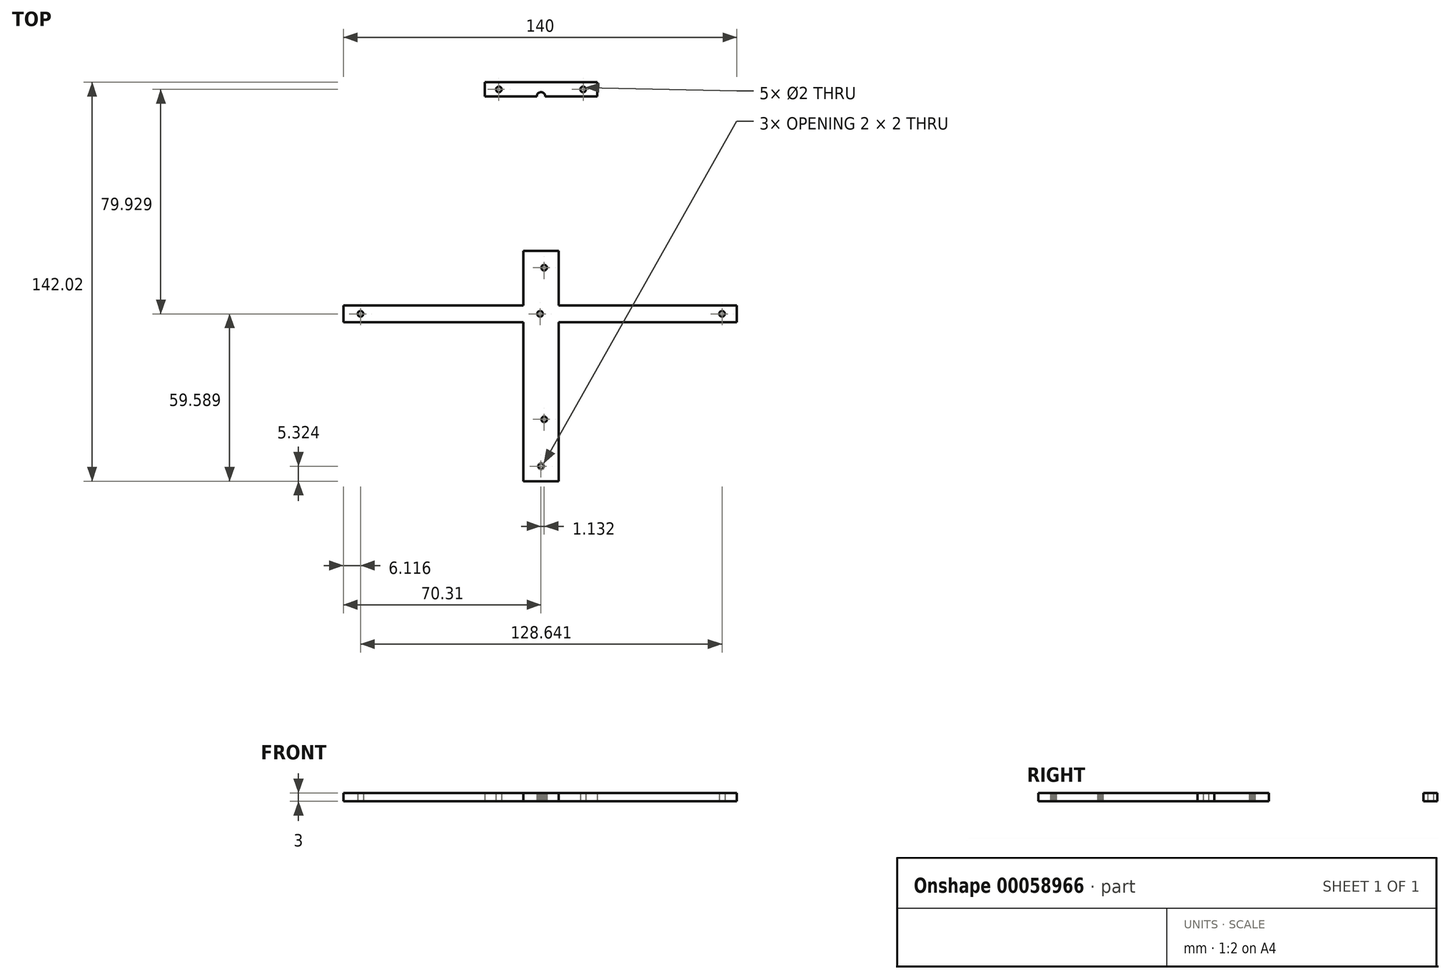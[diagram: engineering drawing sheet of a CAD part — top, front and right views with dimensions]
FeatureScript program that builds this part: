
annotation { "Feature Type Name" : "Feature", "Feature Type Description" : "" }
export const myFeature = defineFeature(function(context is Context, id is Id, definition is map)
    precondition{}
    {
        {
            var Q0;
            Q0=qCreatedBy(makeId("Top.planeOp"),FACE);
            var sketch = newSketch(context, id + "F0", { "sketchPlane" : qUnion([Q0])});
            skLineSegment(sketch, "E0", {"start": v(0.84, 33.8) * mm, "end": v(0.83, 33.92) * mm});
            skLineSegment(sketch, "E1", {"start": v(0.83, 33.92) * mm, "end": v(0.81, 34.04) * mm});
            skLineSegment(sketch, "E2", {"start": v(0.81, 34.04) * mm, "end": v(0.77, 34.16) * mm});
            skLineSegment(sketch, "E3", {"start": v(0.77, 34.16) * mm, "end": v(0.72, 34.28) * mm});
            skLineSegment(sketch, "E4", {"start": v(0.72, 34.28) * mm, "end": v(0.65, 34.38) * mm});
            skLineSegment(sketch, "E5", {"start": v(0.65, 34.38) * mm, "end": v(0.57, 34.48) * mm});
            skLineSegment(sketch, "E6", {"start": v(0.57, 34.48) * mm, "end": v(0.48, 34.57) * mm});
            skLineSegment(sketch, "E7", {"start": v(0.48, 34.57) * mm, "end": v(0.38, 34.64) * mm});
            skLineSegment(sketch, "E8", {"start": v(0.38, 34.64) * mm, "end": v(0.27, 34.7) * mm});
            skLineSegment(sketch, "E9", {"start": v(0.27, 34.7) * mm, "end": v(0.15, 34.75) * mm});
            skLineSegment(sketch, "E10", {"start": v(0.15, 34.75) * mm, "end": v(0.03, 34.78) * mm});
            skLineSegment(sketch, "E11", {"start": v(0.03, 34.78) * mm, "end": v(-0.1, 34.8) * mm});
            skLineSegment(sketch, "E12", {"start": v(-0.1, 34.8) * mm, "end": v(-0.22, 34.8) * mm});
            skLineSegment(sketch, "E13", {"start": v(-0.22, 34.8) * mm, "end": v(-0.35, 34.78) * mm});
            skLineSegment(sketch, "E14", {"start": v(-0.35, 34.78) * mm, "end": v(-0.47, 34.75) * mm});
            skLineSegment(sketch, "E15", {"start": v(-0.58, 34.7) * mm, "end": v(-0.7, 34.64) * mm});
            skLineSegment(sketch, "E16", {"start": v(-0.7, 34.64) * mm, "end": v(-0.8, 34.57) * mm});
            skLineSegment(sketch, "E17", {"start": v(-0.8, 34.57) * mm, "end": v(-0.89, 34.48) * mm});
            skLineSegment(sketch, "E18", {"start": v(-0.89, 34.48) * mm, "end": v(-0.97, 34.38) * mm});
            skLineSegment(sketch, "E19", {"start": v(-0.97, 34.38) * mm, "end": v(-1.03, 34.28) * mm});
            skLineSegment(sketch, "E20", {"start": v(-1.03, 34.28) * mm, "end": v(-1.09, 34.16) * mm});
            skLineSegment(sketch, "E21", {"start": v(-1.09, 34.16) * mm, "end": v(-1.13, 34.04) * mm});
            skLineSegment(sketch, "E22", {"start": v(-1.13, 34.04) * mm, "end": v(-1.15, 33.92) * mm});
            skLineSegment(sketch, "E23", {"start": v(-1.15, 33.92) * mm, "end": v(-1.16, 33.8) * mm});
            skLineSegment(sketch, "E24", {"start": v(-1.16, 33.8) * mm, "end": v(-1.15, 33.67) * mm});
            skLineSegment(sketch, "E25", {"start": v(-1.15, 33.67) * mm, "end": v(-1.13, 33.55) * mm});
            skLineSegment(sketch, "E26", {"start": v(-1.13, 33.55) * mm, "end": v(-1.09, 33.43) * mm});
            skLineSegment(sketch, "E27", {"start": v(-1.09, 33.43) * mm, "end": v(-1.03, 33.31) * mm});
            skLineSegment(sketch, "E28", {"start": v(-1.03, 33.31) * mm, "end": v(-0.97, 33.2) * mm});
            skLineSegment(sketch, "E29", {"start": v(-0.97, 33.2) * mm, "end": v(-0.89, 33.11) * mm});
            skLineSegment(sketch, "E30", {"start": v(-0.89, 33.11) * mm, "end": v(-0.8, 33.03) * mm});
            skLineSegment(sketch, "E31", {"start": v(-0.8, 33.03) * mm, "end": v(-0.7, 32.95) * mm});
            skLineSegment(sketch, "E32", {"start": v(-0.7, 32.95) * mm, "end": v(-0.58, 32.9) * mm});
            skLineSegment(sketch, "E33", {"start": v(-0.58, 32.9) * mm, "end": v(-0.47, 32.85) * mm});
            skLineSegment(sketch, "E34", {"start": v(-0.47, 32.85) * mm, "end": v(-0.35, 32.81) * mm});
            skLineSegment(sketch, "E35", {"start": v(-0.35, 32.81) * mm, "end": v(-0.22, 32.8) * mm});
            skLineSegment(sketch, "E36", {"start": v(-0.22, 32.8) * mm, "end": v(-0.1, 32.8) * mm});
            skLineSegment(sketch, "E37", {"start": v(-0.1, 32.8) * mm, "end": v(0.03, 32.81) * mm});
            skLineSegment(sketch, "E38", {"start": v(0.03, 32.81) * mm, "end": v(0.15, 32.85) * mm});
            skLineSegment(sketch, "E39", {"start": v(0.15, 32.85) * mm, "end": v(0.27, 32.9) * mm});
            skLineSegment(sketch, "E40", {"start": v(0.27, 32.9) * mm, "end": v(0.38, 32.95) * mm});
            skLineSegment(sketch, "E41", {"start": v(0.38, 32.95) * mm, "end": v(0.48, 33.03) * mm});
            skLineSegment(sketch, "E42", {"start": v(0.48, 33.03) * mm, "end": v(0.57, 33.11) * mm});
            skLineSegment(sketch, "E43", {"start": v(0.57, 33.11) * mm, "end": v(0.65, 33.2) * mm});
            skLineSegment(sketch, "E44", {"start": v(0.65, 33.2) * mm, "end": v(0.72, 33.31) * mm});
            skLineSegment(sketch, "E45", {"start": v(0.72, 33.31) * mm, "end": v(0.77, 33.43) * mm});
            skLineSegment(sketch, "E46", {"start": v(0.77, 33.43) * mm, "end": v(0.81, 33.55) * mm});
            skLineSegment(sketch, "E47", {"start": v(0.81, 33.55) * mm, "end": v(0.83, 33.67) * mm});
            skLineSegment(sketch, "E48", {"start": v(0.83, 33.67) * mm, "end": v(0.84, 33.8) * mm});
            skLineSegment(sketch, "E49", {"start": v(-0.29, -36.9) * mm, "end": v(-0.3, -36.78) * mm});
            skLineSegment(sketch, "E50", {"start": v(-0.3, -36.78) * mm, "end": v(-0.32, -36.66) * mm});
            skLineSegment(sketch, "E51", {"start": v(-0.32, -36.66) * mm, "end": v(-0.36, -36.54) * mm});
            skLineSegment(sketch, "E52", {"start": v(-0.36, -36.54) * mm, "end": v(-0.41, -36.42) * mm});
            skLineSegment(sketch, "E53", {"start": v(-0.41, -36.42) * mm, "end": v(-0.48, -36.32) * mm});
            skLineSegment(sketch, "E54", {"start": v(-0.48, -36.32) * mm, "end": v(-0.56, -36.22) * mm});
            skLineSegment(sketch, "E55", {"start": v(-0.56, -36.22) * mm, "end": v(-0.65, -36.14) * mm});
            skLineSegment(sketch, "E56", {"start": v(-0.65, -36.14) * mm, "end": v(-0.75, -36.06) * mm});
            skLineSegment(sketch, "E57", {"start": v(-0.75, -36.06) * mm, "end": v(-0.86, -36) * mm});
            skLineSegment(sketch, "E58", {"start": v(-0.86, -36) * mm, "end": v(-0.98, -35.95) * mm});
            skLineSegment(sketch, "E59", {"start": v(-0.98, -35.95) * mm, "end": v(-1.1, -35.92) * mm});
            skLineSegment(sketch, "E60", {"start": v(-1.1, -35.92) * mm, "end": v(-1.23, -35.9) * mm});
            skLineSegment(sketch, "E61", {"start": v(-1.23, -35.9) * mm, "end": v(-1.35, -35.9) * mm});
            skLineSegment(sketch, "E62", {"start": v(-1.35, -35.9) * mm, "end": v(-1.48, -35.92) * mm});
            skLineSegment(sketch, "E63", {"start": v(-1.48, -35.92) * mm, "end": v(-1.6, -35.95) * mm});
            skLineSegment(sketch, "E64", {"start": v(-1.6, -35.95) * mm, "end": v(-1.72, -36) * mm});
            skLineSegment(sketch, "E65", {"start": v(-1.72, -36) * mm, "end": v(-1.83, -36.06) * mm});
            skLineSegment(sketch, "E66", {"start": v(-1.83, -36.06) * mm, "end": v(-1.93, -36.14) * mm});
            skLineSegment(sketch, "E67", {"start": v(-1.93, -36.14) * mm, "end": v(-2.02, -36.22) * mm});
            skLineSegment(sketch, "E68", {"start": v(-2.02, -36.22) * mm, "end": v(-2.1, -36.32) * mm});
            skLineSegment(sketch, "E69", {"start": v(-2.1, -36.32) * mm, "end": v(-2.17, -36.42) * mm});
            skLineSegment(sketch, "E70", {"start": v(-2.17, -36.42) * mm, "end": v(-2.22, -36.54) * mm});
            skLineSegment(sketch, "E71", {"start": v(-2.22, -36.54) * mm, "end": v(-2.26, -36.66) * mm});
            skLineSegment(sketch, "E72", {"start": v(-2.26, -36.66) * mm, "end": v(-2.28, -36.78) * mm});
            skLineSegment(sketch, "E73", {"start": v(-2.28, -36.78) * mm, "end": v(-2.29, -36.9) * mm});
            skLineSegment(sketch, "E74", {"start": v(-2.29, -36.9) * mm, "end": v(-2.28, -37.03) * mm});
            skLineSegment(sketch, "E75", {"start": v(-2.28, -37.03) * mm, "end": v(-2.26, -37.15) * mm});
            skLineSegment(sketch, "E76", {"start": v(-2.26, -37.15) * mm, "end": v(-2.22, -37.27) * mm});
            skLineSegment(sketch, "E77", {"start": v(-2.22, -37.27) * mm, "end": v(-2.17, -37.39) * mm});
            skLineSegment(sketch, "E78", {"start": v(-2.17, -37.39) * mm, "end": v(-2.1, -37.5) * mm});
            skLineSegment(sketch, "E79", {"start": v(-2.1, -37.5) * mm, "end": v(-2.02, -37.6) * mm});
            skLineSegment(sketch, "E80", {"start": v(-2.02, -37.6) * mm, "end": v(-1.93, -37.68) * mm});
            skLineSegment(sketch, "E81", {"start": v(-1.93, -37.68) * mm, "end": v(-1.83, -37.75) * mm});
            skLineSegment(sketch, "E82", {"start": v(-1.83, -37.75) * mm, "end": v(-1.72, -37.81) * mm});
            skLineSegment(sketch, "E83", {"start": v(-1.72, -37.81) * mm, "end": v(-1.6, -37.86) * mm});
            skLineSegment(sketch, "E84", {"start": v(-1.6, -37.86) * mm, "end": v(-1.48, -37.89) * mm});
            skLineSegment(sketch, "E85", {"start": v(-1.48, -37.89) * mm, "end": v(-1.35, -37.9) * mm});
            skLineSegment(sketch, "E86", {"start": v(-1.35, -37.9) * mm, "end": v(-1.23, -37.9) * mm});
            skLineSegment(sketch, "E87", {"start": v(-1.23, -37.9) * mm, "end": v(-1.1, -37.89) * mm});
            skLineSegment(sketch, "E88", {"start": v(-1.1, -37.89) * mm, "end": v(-0.98, -37.86) * mm});
            skLineSegment(sketch, "E89", {"start": v(-0.98, -37.86) * mm, "end": v(-0.86, -37.81) * mm});
            skLineSegment(sketch, "E90", {"start": v(-0.86, -37.81) * mm, "end": v(-0.75, -37.75) * mm});
            skLineSegment(sketch, "E91", {"start": v(-0.75, -37.75) * mm, "end": v(-0.65, -37.68) * mm});
            skLineSegment(sketch, "E92", {"start": v(-0.65, -37.68) * mm, "end": v(-0.56, -37.6) * mm});
            skLineSegment(sketch, "E93", {"start": v(-0.56, -37.6) * mm, "end": v(-0.48, -37.5) * mm});
            skLineSegment(sketch, "E94", {"start": v(-0.48, -37.5) * mm, "end": v(-0.41, -37.39) * mm});
            skLineSegment(sketch, "E95", {"start": v(-0.41, -37.39) * mm, "end": v(-0.36, -37.27) * mm});
            skLineSegment(sketch, "E96", {"start": v(-0.36, -37.27) * mm, "end": v(-0.32, -37.15) * mm});
            skLineSegment(sketch, "E97", {"start": v(-0.32, -37.15) * mm, "end": v(-0.3, -37.03) * mm});
            skLineSegment(sketch, "E98", {"start": v(-0.3, -37.03) * mm, "end": v(-0.29, -36.9) * mm});
            skLineSegment(sketch, "E99", {"start": v(0.84, -20.2) * mm, "end": v(0.83, -20.08) * mm});
            skLineSegment(sketch, "E100", {"start": v(0.83, -20.08) * mm, "end": v(0.81, -19.96) * mm});
            skLineSegment(sketch, "E101", {"start": v(0.81, -19.96) * mm, "end": v(0.77, -19.84) * mm});
            skLineSegment(sketch, "E102", {"start": v(0.77, -19.84) * mm, "end": v(0.72, -19.72) * mm});
            skLineSegment(sketch, "E103", {"start": v(0.72, -19.72) * mm, "end": v(0.65, -19.62) * mm});
            skLineSegment(sketch, "E104", {"start": v(0.65, -19.62) * mm, "end": v(0.57, -19.52) * mm});
            skLineSegment(sketch, "E105", {"start": v(0.57, -19.52) * mm, "end": v(0.48, -19.43) * mm});
            skLineSegment(sketch, "E106", {"start": v(0.48, -19.43) * mm, "end": v(0.38, -19.36) * mm});
            skLineSegment(sketch, "E107", {"start": v(0.38, -19.36) * mm, "end": v(0.27, -19.3) * mm});
            skLineSegment(sketch, "E108", {"start": v(0.27, -19.3) * mm, "end": v(0.15, -19.25) * mm});
            skLineSegment(sketch, "E109", {"start": v(0.15, -19.25) * mm, "end": v(0.03, -19.22) * mm});
            skLineSegment(sketch, "E110", {"start": v(0.03, -19.22) * mm, "end": v(-0.1, -19.2) * mm});
            skLineSegment(sketch, "E111", {"start": v(-0.1, -19.2) * mm, "end": v(-0.22, -19.2) * mm});
            skLineSegment(sketch, "E112", {"start": v(-0.22, -19.2) * mm, "end": v(-0.35, -19.22) * mm});
            skLineSegment(sketch, "E113", {"start": v(-0.35, -19.22) * mm, "end": v(-0.47, -19.25) * mm});
            skLineSegment(sketch, "E114", {"start": v(-0.47, -19.25) * mm, "end": v(-0.58, -19.3) * mm});
            skLineSegment(sketch, "E115", {"start": v(-0.58, -19.3) * mm, "end": v(-0.7, -19.36) * mm});
            skLineSegment(sketch, "E116", {"start": v(-0.7, -19.36) * mm, "end": v(-0.8, -19.43) * mm});
            skLineSegment(sketch, "E117", {"start": v(-0.8, -19.43) * mm, "end": v(-0.89, -19.52) * mm});
            skLineSegment(sketch, "E118", {"start": v(-0.89, -19.52) * mm, "end": v(-0.97, -19.62) * mm});
            skLineSegment(sketch, "E119", {"start": v(-0.97, -19.62) * mm, "end": v(-1.03, -19.72) * mm});
            skLineSegment(sketch, "E120", {"start": v(-1.03, -19.72) * mm, "end": v(-1.09, -19.84) * mm});
            skLineSegment(sketch, "E121", {"start": v(-1.09, -19.84) * mm, "end": v(-1.13, -19.96) * mm});
            skLineSegment(sketch, "E122", {"start": v(-1.13, -19.96) * mm, "end": v(-1.15, -20.08) * mm});
            skLineSegment(sketch, "E123", {"start": v(-1.15, -20.08) * mm, "end": v(-1.16, -20.2) * mm});
            skLineSegment(sketch, "E124", {"start": v(-1.16, -20.2) * mm, "end": v(-1.15, -20.33) * mm});
            skLineSegment(sketch, "E125", {"start": v(-1.15, -20.33) * mm, "end": v(-1.13, -20.45) * mm});
            skLineSegment(sketch, "E126", {"start": v(-1.13, -20.45) * mm, "end": v(-1.09, -20.57) * mm});
            skLineSegment(sketch, "E127", {"start": v(-1.09, -20.57) * mm, "end": v(-1.03, -20.69) * mm});
            skLineSegment(sketch, "E128", {"start": v(-1.03, -20.69) * mm, "end": v(-0.97, -20.8) * mm});
            skLineSegment(sketch, "E129", {"start": v(-0.97, -20.8) * mm, "end": v(-0.89, -20.89) * mm});
            skLineSegment(sketch, "E130", {"start": v(-0.89, -20.89) * mm, "end": v(-0.8, -20.97) * mm});
            skLineSegment(sketch, "E131", {"start": v(-0.8, -20.97) * mm, "end": v(-0.7, -21.05) * mm});
            skLineSegment(sketch, "E132", {"start": v(-0.7, -21.05) * mm, "end": v(-0.58, -21.1) * mm});
            skLineSegment(sketch, "E133", {"start": v(-0.58, -21.1) * mm, "end": v(-0.47, -21.15) * mm});
            skLineSegment(sketch, "E134", {"start": v(-0.47, -21.15) * mm, "end": v(-0.35, -21.19) * mm});
            skLineSegment(sketch, "E135", {"start": v(-0.35, -21.19) * mm, "end": v(-0.22, -21.2) * mm});
            skLineSegment(sketch, "E136", {"start": v(-0.22, -21.2) * mm, "end": v(-0.1, -21.2) * mm});
            skLineSegment(sketch, "E137", {"start": v(-0.1, -21.2) * mm, "end": v(0.03, -21.19) * mm});
            skLineSegment(sketch, "E138", {"start": v(0.03, -21.19) * mm, "end": v(0.15, -21.15) * mm});
            skLineSegment(sketch, "E139", {"start": v(0.15, -21.15) * mm, "end": v(0.27, -21.1) * mm});
            skLineSegment(sketch, "E140", {"start": v(0.27, -21.1) * mm, "end": v(0.38, -21.05) * mm});
            skLineSegment(sketch, "E141", {"start": v(0.38, -21.05) * mm, "end": v(0.48, -20.97) * mm});
            skLineSegment(sketch, "E142", {"start": v(0.48, -20.97) * mm, "end": v(0.57, -20.89) * mm});
            skLineSegment(sketch, "E143", {"start": v(0.57, -20.89) * mm, "end": v(0.65, -20.8) * mm});
            skLineSegment(sketch, "E144", {"start": v(0.65, -20.8) * mm, "end": v(0.72, -20.69) * mm});
            skLineSegment(sketch, "E145", {"start": v(0.72, -20.69) * mm, "end": v(0.77, -20.57) * mm});
            skLineSegment(sketch, "E146", {"start": v(0.77, -20.57) * mm, "end": v(0.81, -20.45) * mm});
            skLineSegment(sketch, "E147", {"start": v(0.81, -20.45) * mm, "end": v(0.83, -20.33) * mm});
            skLineSegment(sketch, "E148", {"start": v(0.83, -20.33) * mm, "end": v(0.84, -20.2) * mm});
            skLineSegment(sketch, "E149", {"start": v(-0.47, 34.75) * mm, "end": v(-0.58, 34.7) * mm});
            skLineSegment(sketch, "E150", {"start": v(28.34, 33.8) * mm, "end": v(28.33, 33.92) * mm});
            skLineSegment(sketch, "E151", {"start": v(28.33, 33.92) * mm, "end": v(28.31, 34.04) * mm});
            skLineSegment(sketch, "E152", {"start": v(28.31, 34.04) * mm, "end": v(28.27, 34.16) * mm});
            skLineSegment(sketch, "E153", {"start": v(28.27, 34.16) * mm, "end": v(28.22, 34.28) * mm});
            skLineSegment(sketch, "E154", {"start": v(28.22, 34.28) * mm, "end": v(28.15, 34.38) * mm});
            skLineSegment(sketch, "E155", {"start": v(28.15, 34.38) * mm, "end": v(28.07, 34.48) * mm});
            skLineSegment(sketch, "E156", {"start": v(28.07, 34.48) * mm, "end": v(27.98, 34.57) * mm});
            skLineSegment(sketch, "E157", {"start": v(27.98, 34.57) * mm, "end": v(27.88, 34.64) * mm});
            skLineSegment(sketch, "E158", {"start": v(27.88, 34.64) * mm, "end": v(27.77, 34.7) * mm});
            skLineSegment(sketch, "E159", {"start": v(27.77, 34.7) * mm, "end": v(27.65, 34.75) * mm});
            skLineSegment(sketch, "E160", {"start": v(27.65, 34.75) * mm, "end": v(27.53, 34.78) * mm});
            skLineSegment(sketch, "E161", {"start": v(27.53, 34.78) * mm, "end": v(27.4, 34.8) * mm});
            skLineSegment(sketch, "E162", {"start": v(27.4, 34.8) * mm, "end": v(27.28, 34.8) * mm});
            skLineSegment(sketch, "E163", {"start": v(27.28, 34.8) * mm, "end": v(27.15, 34.78) * mm});
            skLineSegment(sketch, "E164", {"start": v(27.15, 34.78) * mm, "end": v(27.03, 34.75) * mm});
            skLineSegment(sketch, "E165", {"start": v(27.03, 34.75) * mm, "end": v(26.92, 34.7) * mm});
            skLineSegment(sketch, "E166", {"start": v(26.92, 34.7) * mm, "end": v(26.8, 34.64) * mm});
            skLineSegment(sketch, "E167", {"start": v(26.8, 34.64) * mm, "end": v(26.7, 34.57) * mm});
            skLineSegment(sketch, "E168", {"start": v(26.7, 34.57) * mm, "end": v(26.61, 34.48) * mm});
            skLineSegment(sketch, "E169", {"start": v(26.61, 34.48) * mm, "end": v(26.53, 34.38) * mm});
            skLineSegment(sketch, "E170", {"start": v(26.53, 34.38) * mm, "end": v(26.47, 34.28) * mm});
            skLineSegment(sketch, "E171", {"start": v(26.47, 34.28) * mm, "end": v(26.41, 34.16) * mm});
            skLineSegment(sketch, "E172", {"start": v(26.41, 34.16) * mm, "end": v(26.37, 34.04) * mm});
            skLineSegment(sketch, "E173", {"start": v(26.37, 34.04) * mm, "end": v(26.35, 33.92) * mm});
            skLineSegment(sketch, "E174", {"start": v(26.35, 33.92) * mm, "end": v(26.34, 33.8) * mm});
            skLineSegment(sketch, "E175", {"start": v(26.34, 33.8) * mm, "end": v(26.35, 33.67) * mm});
            skLineSegment(sketch, "E176", {"start": v(26.35, 33.67) * mm, "end": v(26.37, 33.55) * mm});
            skLineSegment(sketch, "E177", {"start": v(26.37, 33.55) * mm, "end": v(26.41, 33.43) * mm});
            skLineSegment(sketch, "E178", {"start": v(26.41, 33.43) * mm, "end": v(26.47, 33.31) * mm});
            skLineSegment(sketch, "E179", {"start": v(26.47, 33.31) * mm, "end": v(26.53, 33.2) * mm});
            skLineSegment(sketch, "E180", {"start": v(26.53, 33.2) * mm, "end": v(26.61, 33.11) * mm});
            skLineSegment(sketch, "E181", {"start": v(26.61, 33.11) * mm, "end": v(26.7, 33.03) * mm});
            skLineSegment(sketch, "E182", {"start": v(26.7, 33.03) * mm, "end": v(26.8, 32.95) * mm});
            skLineSegment(sketch, "E183", {"start": v(26.8, 32.95) * mm, "end": v(26.92, 32.9) * mm});
            skLineSegment(sketch, "E184", {"start": v(26.92, 32.9) * mm, "end": v(27.03, 32.85) * mm});
            skLineSegment(sketch, "E185", {"start": v(27.03, 32.85) * mm, "end": v(27.15, 32.81) * mm});
            skLineSegment(sketch, "E186", {"start": v(27.15, 32.81) * mm, "end": v(27.28, 32.8) * mm});
            skLineSegment(sketch, "E187", {"start": v(27.28, 32.8) * mm, "end": v(27.4, 32.8) * mm});
            skLineSegment(sketch, "E188", {"start": v(27.4, 32.8) * mm, "end": v(27.53, 32.81) * mm});
            skLineSegment(sketch, "E189", {"start": v(27.53, 32.81) * mm, "end": v(27.65, 32.85) * mm});
            skLineSegment(sketch, "E190", {"start": v(27.65, 32.85) * mm, "end": v(27.77, 32.9) * mm});
            skLineSegment(sketch, "E191", {"start": v(27.77, 32.9) * mm, "end": v(27.88, 32.95) * mm});
            skLineSegment(sketch, "E192", {"start": v(27.88, 32.95) * mm, "end": v(27.98, 33.03) * mm});
            skLineSegment(sketch, "E193", {"start": v(27.98, 33.03) * mm, "end": v(28.07, 33.11) * mm});
            skLineSegment(sketch, "E194", {"start": v(28.07, 33.11) * mm, "end": v(28.15, 33.2) * mm});
            skLineSegment(sketch, "E195", {"start": v(28.15, 33.2) * mm, "end": v(28.22, 33.31) * mm});
            skLineSegment(sketch, "E196", {"start": v(28.22, 33.31) * mm, "end": v(28.27, 33.43) * mm});
            skLineSegment(sketch, "E197", {"start": v(28.27, 33.43) * mm, "end": v(28.31, 33.55) * mm});
            skLineSegment(sketch, "E198", {"start": v(28.31, 33.55) * mm, "end": v(28.33, 33.67) * mm});
            skLineSegment(sketch, "E199", {"start": v(28.33, 33.67) * mm, "end": v(28.34, 33.8) * mm});
            skLineSegment(sketch, "E200", {"start": v(-2.29, -36.9) * mm, "end": v(-0.29, -36.9) * mm, "construction": true});
            skPoint(sketch, "E201", {"position": v(-1.29, -36.9) * mm});
            skLineSegment(sketch, "E202.bottom", {"start": v(-1.29, -42.23) * mm, "end": v(-7.55, -42.23) * mm});
            skLineSegment(sketch, "E202.top", {"start": v(-1.29, 39.79) * mm, "end": v(-7.55, 39.79) * mm});
            skLineSegment(sketch, "E202.right", {"start": v(-7.55, -42.23) * mm, "end": v(-7.55, 39.79) * mm});
            skPoint(sketch, "E203.oppositeSnap0", {"position": v(-4.42, -42.23) * mm});
            skLineSegment(sketch, "E203.bottom", {"start": v(-1.29, 39.79) * mm, "end": v(4.98, 39.79) * mm});
            skLineSegment(sketch, "E203.top", {"start": v(-1.29, -42.23) * mm, "end": v(4.98, -42.23) * mm});
            skLineSegment(sketch, "E203.right", {"start": v(4.98, 28.88) * mm, "end": v(4.98, -42.23) * mm});
            skLineSegment(sketch, "E204.bottom", {"start": v(34.68, 39.79) * mm, "end": v(4.98, 39.79) * mm});
            skLineSegment(sketch, "E204.top", {"start": v(34.68, 28.88) * mm, "end": v(4.98, 28.88) * mm});
            skLineSegment(sketch, "E204.left", {"start": v(34.68, 39.79) * mm, "end": v(34.68, 28.88) * mm});
            skPoint(sketch, "E205", {"position": v(-1.6, 17.36) * mm});
            skLineSegment(sketch, "E206.bottom", {"start": v(-1.6, 20.36) * mm, "end": v(-71.6, 20.36) * mm});
            skLineSegment(sketch, "E206.top", {"start": v(-1.6, 14.36) * mm, "end": v(-71.6, 14.36) * mm});
            skLineSegment(sketch, "E206.left", {"start": v(-1.6, 20.36) * mm, "end": v(-1.6, 14.36) * mm});
            skLineSegment(sketch, "E206.right", {"start": v(-71.6, 20.36) * mm, "end": v(-71.6, 14.36) * mm});
            skLineSegment(sketch, "E207.bottom", {"start": v(-1.6, 20.36) * mm, "end": v(68.4, 20.36) * mm});
            skLineSegment(sketch, "E207.top", {"start": v(-1.6, 14.36) * mm, "end": v(68.4, 14.36) * mm});
            skLineSegment(sketch, "E207.right", {"start": v(68.4, 20.36) * mm, "end": v(68.4, 14.36) * mm});
            skLineSegment(sketch, "E208", {"start": v(4.98, 39.79) * mm, "end": v(4.98, 28.88) * mm});
            skLineSegment(sketch, "E209", {"start": v(-71.6, 17.36) * mm, "end": v(68.4, 17.36) * mm, "construction": true});
            skCircle(sketch, "E210", {"center": v(63.16, 17.36) * mm, "radius": 1 * mm});
            skCircle(sketch, "E211", {"center": v(-65.48, 17.36) * mm, "radius": 1 * mm});
            skLineSegment(sketch, "E212", {"start": v(-1.16, 33.8) * mm, "end": v(0.84, 33.8) * mm, "construction": true});
            skPoint(sketch, "E213", {"position": v(-0.16, 33.8) * mm});
            skLineSegment(sketch, "E214.bottom", {"start": v(-7.55, 39.79) * mm, "end": v(4.98, 39.79) * mm});
            skLineSegment(sketch, "E214.top", {"start": v(-7.55, 99.79) * mm, "end": v(4.98, 99.79) * mm});
            skLineSegment(sketch, "E214.left", {"start": v(-7.55, 39.79) * mm, "end": v(-7.55, 99.79) * mm});
            skLineSegment(sketch, "E214.right", {"start": v(4.98, 39.79) * mm, "end": v(4.98, 99.79) * mm});
            skCircle(sketch, "E215", {"center": v(-1.29, 94.79) * mm, "radius": 1.5 * mm});
            skPoint(sketch, "E215.centerSnap0", {"position": v(-1.29, 99.79) * mm});
            skLineSegment(sketch, "E216.bottom", {"start": v(-21.29, 99.79) * mm, "end": v(18.71, 99.79) * mm});
            skLineSegment(sketch, "E216.top", {"start": v(-21.29, 94.79) * mm, "end": v(18.71, 94.79) * mm});
            skLineSegment(sketch, "E216.left", {"start": v(-21.29, 99.79) * mm, "end": v(-21.29, 94.79) * mm});
            skLineSegment(sketch, "E216.right", {"start": v(18.71, 99.79) * mm, "end": v(18.71, 94.79) * mm});
            skCircle(sketch, "E217", {"center": v(-16.29, 97.29) * mm, "radius": 1 * mm});
            skPoint(sketch, "E217.centerSnap0", {"position": v(-21.29, 97.29) * mm});
            skCircle(sketch, "E218", {"center": v(13.71, 97.29) * mm, "radius": 1 * mm});
            skPoint(sketch, "E218.centerSnap0", {"position": v(18.71, 97.29) * mm});
            skCircle(sketch, "E219", {"center": v(-1.6, 17.36) * mm, "radius": 1 * mm});
            skSolve(sketch);
        }
        {
            var Q0;
            Q0=makeQuery(id+"F0.imprint","IMPRINT",FACE,{"disambiguationData":[TD([[makeQuery(id+"F0.imprint","IMPRINT",EDGE,{"derivedFrom":sQuery(id+"F0.wireOp",EDGE,"E49")}),-1.0]])]});
            var Q1;
            {var subQ0=sQuery(id+"F0.wireOp",EDGE,"d9d795a4-12a4-42d5-b6af-be746a3b56d2");Q1=makeQuery(id+"F0.imprint","IMPRINT",FACE,{"disambiguationData":[TD([[makeQuery(id+"F0.imprint","IMPRINT",EDGE,{"derivedFrom":subQ0}),-1.0]])]});}
            var Q2;
            Q2=makeQuery(id+"F0.imprint","IMPRINT",FACE,{"disambiguationData":[TD([[makeQuery(id+"F0.imprint","IMPRINT",EDGE,{"derivedFrom":sQuery(id+"F0.wireOp",EDGE,"044ca1f0-f9e8-4e3d-8bcb-43c99246160e")}),-1.0]])]});
            var Q3;
            Q3=makeQuery(id+"F0.imprint","IMPRINT",FACE,{"disambiguationData":[TD([[makeQuery(id+"F0.imprint","IMPRINT",EDGE,{"derivedFrom":sQuery(id+"F0.wireOp",EDGE,"E0")}),-1.0]])]});
            var Q4;
            {var subQ5=sQuery(id+"F0.wireOp",EDGE,"E206.right");Q4=makeQuery(id+"F0.imprint","IMPRINT",FACE,{"disambiguationData":[TD([[makeQuery(id+"F0.imprint","IMPRINT",EDGE,{"derivedFrom":subQ5}),1.0]])]});}
            var Q5;
            {var subQ5=sQuery(id+"F0.wireOp",EDGE,"E207.right");Q5=makeQuery(id+"F0.imprint","IMPRINT",FACE,{"disambiguationData":[TD([[makeQuery(id+"F0.imprint","IMPRINT",EDGE,{"derivedFrom":subQ5}),-1.0]])]});}
            var Q6;
            {var subQ4=sQuery(id+"F0.wireOp",EDGE,"E206.top");var subQ6=sQuery(id+"F0.wireOp",EDGE,"E202.right");var subQ7=makeQuery(id+"F0.imprint","INTERSECT",VERTEX,{"derivedFrom":[subQ6,subQ4]});Q6=makeQuery(id+"F0.imprint","IMPRINT",FACE,{"disambiguationData":[TD([[makeQuery(id+"F0.imprint","IMPRINT",EDGE,{"disambiguationData":[TD([[subQ7,-1.0]])],"derivedFrom":subQ6}),-1.0]])]});}
            var Q7;
            {var subQ3=sQuery(id+"F0.wireOp",EDGE,"E203.right");var subQ5=sQuery(id+"F0.wireOp",EDGE,"E207.bottom");var subQ7=makeQuery(id+"F0.imprint","INTERSECT",VERTEX,{"derivedFrom":[subQ3,subQ5]});Q7=makeQuery(id+"F0.imprint","IMPRINT",FACE,{"disambiguationData":[TD([[makeQuery(id+"F0.imprint","IMPRINT",EDGE,{"disambiguationData":[TD([[subQ7,-1.0]])],"derivedFrom":subQ3}),-1.0]])]});}
            var Q8;
            {var subQ1=sQuery(id+"F0.wireOp",EDGE,"E214.bottom");var subQ8=makeQuery(id+"F0.imprint","IMPRINT",VERTEX,{"derivedFrom":subQ1});Q8=makeQuery(id+"F0.imprint","IMPRINT",FACE,{"disambiguationData":[TD([[makeQuery(id+"F0.imprint","IMPRINT",EDGE,{"disambiguationData":[TD([[subQ8,1.0]])],"derivedFrom":subQ1}),1.0]])]});}
            var Q9;
            {var subQ0=sQuery(id+"F0.wireOp",EDGE,"E214.top");Q9=makeQuery(id+"F0.imprint","IMPRINT",FACE,{"disambiguationData":[TD([[makeQuery(id+"F0.imprint","IMPRINT",EDGE,{"derivedFrom":subQ0}),1.0]])]});}
            var Q10;
            {var subQ5=sQuery(id+"F0.wireOp",EDGE,"E214.top");Q10=makeQuery(id+"F0.imprint","IMPRINT",FACE,{"disambiguationData":[TD([[makeQuery(id+"F0.imprint","IMPRINT",EDGE,{"derivedFrom":subQ5}),-1.0]])]});}
            extrude(context, id + "F1", {"entities" : qUnion([Q0, Q1, Q2, Q3, Q4, Q5, Q6, Q7, Q8, Q9, Q10]), "depth" : 3 * mm});
        }
    });
